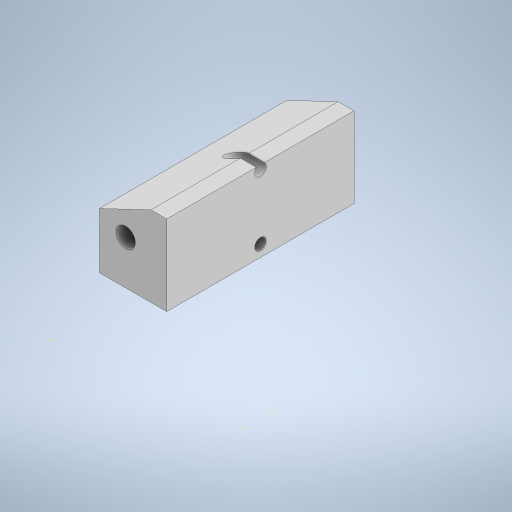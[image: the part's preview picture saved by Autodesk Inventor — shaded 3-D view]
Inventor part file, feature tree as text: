
AUTODESK INVENTOR PART (.ipt)
format: ipt  version: 2024 (Build 280153000, 153)  size: 568,832 bytes
history: native  units: mm
features: sketch x27, extrude x22, move_body x4, chamfer x3, plane x3, split x3, boolean_combine x2, other x1, fillet x1, imported_body x1
ambient origin geometry x8: Origin, YZ Plane, XZ Plane, XY Plane, X Axis, Y Axis, Z Axis, Center Point
bodies: Solid1 (feature_tree), Solid2 (feature_tree), Solid3 (feature_tree), Solid4 (feature_tree), Solid5 (feature_tree), Solid6 (feature_tree), Solid7 (feature_tree), Solid8 (feature_tree)
feature tree (67):
  other  "Repaired Geometry1"
  extrude  "Extrusion1"  Depth=16.0mm
  sketch  "Sketch2"  dims[d2=15.0mm d3=0.0mm d4=10.0mm]
  extrude  "Extrusion2"  Depth=10.0mm
  chamfer  "Chamfer1"  Distance=21.25mm
  extrude  "Extrusion3"  Depth=10.0mm TaperAngle=0.0deg
  extrude  "Extrusion4"  Depth=11.5mm TaperAngle=0.0deg
  extrude  "Extrusion5"  Depth=1.0mm TaperAngle=0.0deg
  chamfer  "Chamfer2"  Distance=6.0mm Angle=45.0deg
  sketch  "Sketch6"  dims[d14=7.0mm d15=11.5mm d16=0.0mm]
  extrude  "Extrusion6"  Depth=9.0mm
  extrude  "Extrusion7"  Depth=11.5mm TaperAngle=0.0deg
  chamfer  "Chamfer3"  Distance=11.5mm Angle=45.0deg
  sketch  "Sketch9"  dims[d26=3.3mm d27=45.25mm d28=0.0mm d29=11.5mm d30=5.5mm d31=45.0deg]
  extrude  "Extrusion8"  Depth=65.75mm TaperAngle=0.0deg
  extrude  "Extrusion9"  Depth=9.0mm TaperAngle=0.0deg
  extrude  "Extrusion10"  Depth=13.0mm TaperAngle=0.0deg
  sketch  "Sketch13"  dims[d43=24.0mm d44=21.0mm d45=0.0mm]
  extrude  "Extrusion11"  Depth=24.0mm TaperAngle=0.0deg
  extrude  "Extrusion12"  TaperAngle=0.0deg  [1 undecoded]
  extrude  "Extrusion13"  Depth=6.0mm TaperAngle=0.0deg
  plane  "Work Plane1"
  split  "Split1"
  move_body  "Move Body1"
  extrude  "Extrusion14"  Depth=0.5mm TaperAngle=0.0deg
  move_body  "Move Body2"
  fillet  "Fillet1"  Radius=10.0mm
  extrude  "Extrusion15"  Depth=10.0mm TaperAngle=0.0deg
  sketch  "Sketch19"  dims[d71=29.5mm d72=0.0mm d73=13.75mm]
  sketch  "Sketch20"  dims[d74=26.0mm d75=0.0mm d76=-5.0mm d77=0.0mm d78=0.0mm]
  extrude  "Extrusion16"  Depth=1.0mm
  extrude  "Extrusion18"  Depth=13.75mm
  extrude  "Extrusion19"  TaperAngle=0.0deg  [1 undecoded]
  sketch  "Sketch23"  dims[d86=11.5mm d87=0.0mm d88=11.5mm d89=0.0mm]
  sketch  "Sketch24"
  extrude  "Extrusion20"  TaperAngle=0.0deg  [1 undecoded]
  plane  "Work Plane2"
  boolean_combine  "Combine1"
  split  "Split2"
  extrude  "Extrusion21"  Depth=11.5mm TaperAngle=0.0deg
  move_body  "Move Body3"
  boolean_combine  "Combine2"
  plane  "Work Plane3"
  split  "Split3"
  move_body  "Move Body4"
  extrude  "Extrusion23"  [1 undecoded]
  extrude  "Extrusion24"  [1 undecoded]
  sketch  "Sketch1"  dims[d0=36.0mm d1=16.0mm]
  sketch  "Sketch3"  dims[d5=10.0mm]
  sketch  "Sketch4"  dims[d6=3.3mm d7=21.25mm d8=0.0mm]
  sketch  "Sketch5"  dims[d9=10.0mm d10=5.5mm d11=45.0deg d12=10.0mm d13=0.0mm]
  sketch  "Sketch7"  dims[d17=3.3mm d18=1.0mm d19=0.0mm d20=6.0mm d21=11.5mm d22=45.0deg]
  sketch  "Sketch8"  dims[d23=15.0mm d24=0.0mm d25=9.0mm]
  sketch  "Sketch10"  dims[d32=2.0mm d33=65.75mm d34=0.0mm]
  sketch  "Sketch11"  dims[d35=0.5mm d36=0.0mm d37=9.0mm d38=0.0mm]
  sketch  "Sketch12"  dims[d39=0.5mm d40=0.0mm d41=13.0mm d42=0.0mm]
  sketch  "Sketch14"  dims[d46=12.25mm d47=-12.0mm d48=0.0mm d49=0.0mm]
  sketch  "Sketch15"  dims[d50=30.0mm d51=0.0mm d52=6.0mm d53=0.0mm d54=0.0mm d55=4.0mm]
  sketch  "Sketch16"  dims[d56=0.5mm d57=0.0mm d58=0.5mm d59=0.0mm d64=10.0mm d65=0.0mm]
  sketch  "Sketch17"  dims[d66=3.0mm d67=10.0mm d68=0.0mm]
  sketch  "Sketch18"  dims[d69=1.0mm d70=31.0mm]
  sketch  "Sketch22"  dims[d79=0.0mm d80=0.0mm d81=0.0mm d82=-30.0mm]
  sketch  "Sketch25"
  sketch  "Sketch26"
  imported_body  "Base1"
  sketch  "Sketch28"
  sketch  "Sketch29"
note: 5 required parameter values undecoded (feature->parameter linkage not recoverable at this tier; creation-order binding heuristic only, values carry confidence <= 0.55)
